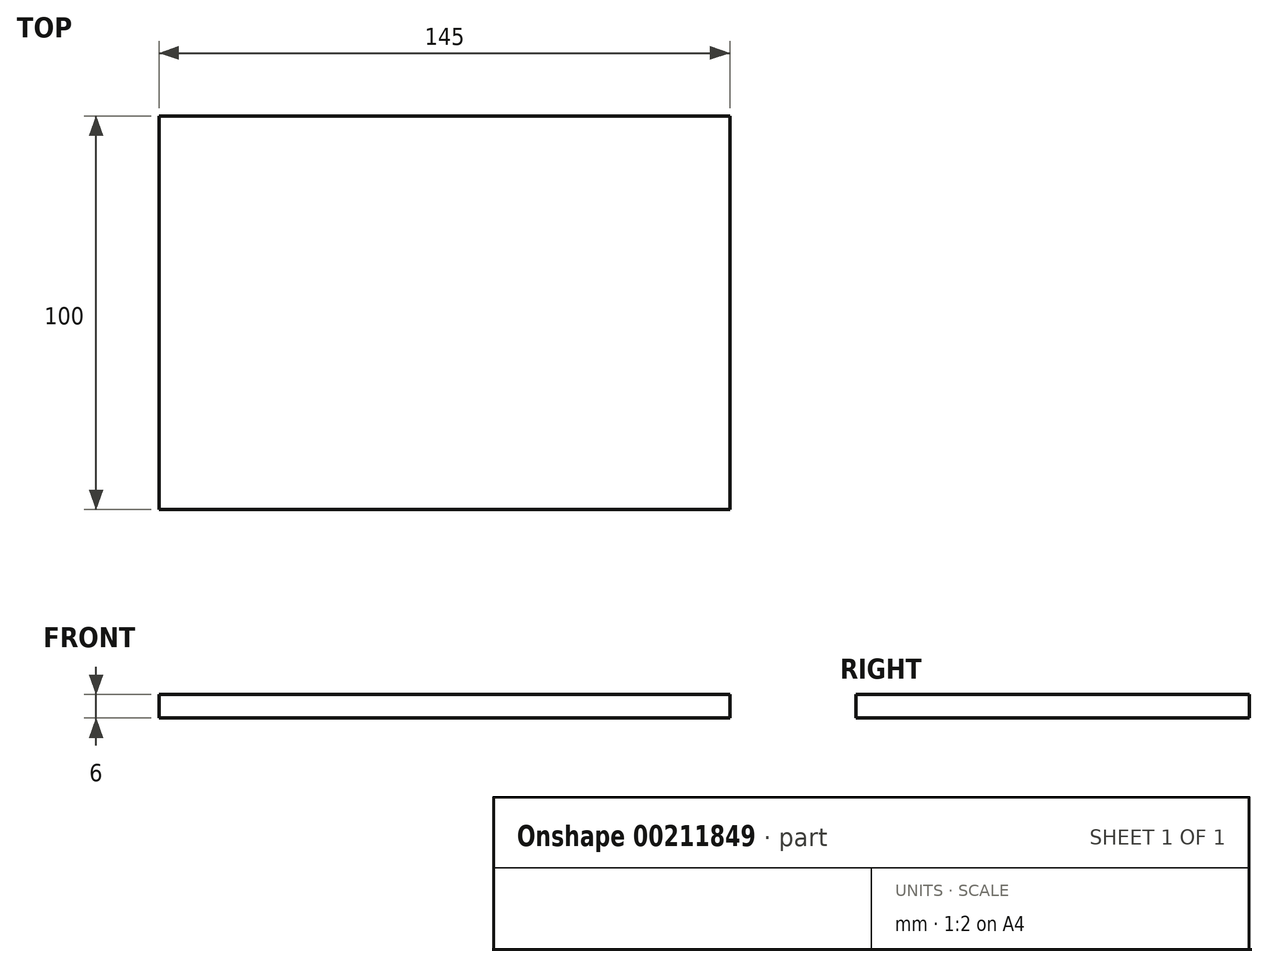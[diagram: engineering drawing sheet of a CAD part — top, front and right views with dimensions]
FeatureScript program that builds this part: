
annotation { "Feature Type Name" : "Feature", "Feature Type Description" : "" }
export const myFeature = defineFeature(function(context is Context, id is Id, definition is map)
    precondition{}
    {
        {
            var Q0;
            Q0=qCreatedBy(makeId("Top.planeOp"),FACE);
            var sketch = newSketch(context, id + "F0", { "sketchPlane" : qUnion([Q0])});
            skLineSegment(sketch, "E0.bottom", {"start": v(0, 0) * mm, "end": v(145, 0) * mm});
            skLineSegment(sketch, "E0.top", {"start": v(0, 100) * mm, "end": v(145, 100) * mm});
            skLineSegment(sketch, "E0.left", {"start": v(0, 0) * mm, "end": v(0, 100) * mm});
            skLineSegment(sketch, "E0.right", {"start": v(145, 0) * mm, "end": v(145, 100) * mm});
            skSolve(sketch);
        }
        {
            var Q0;
            Q0 = qSketchRegion(id + "F0", true);
            extrude(context, id + "F1", {"entities" : qUnion([Q0]), "depth" : 6 * mm, "offsetDistance" : 25 * mm});
        }
    });
